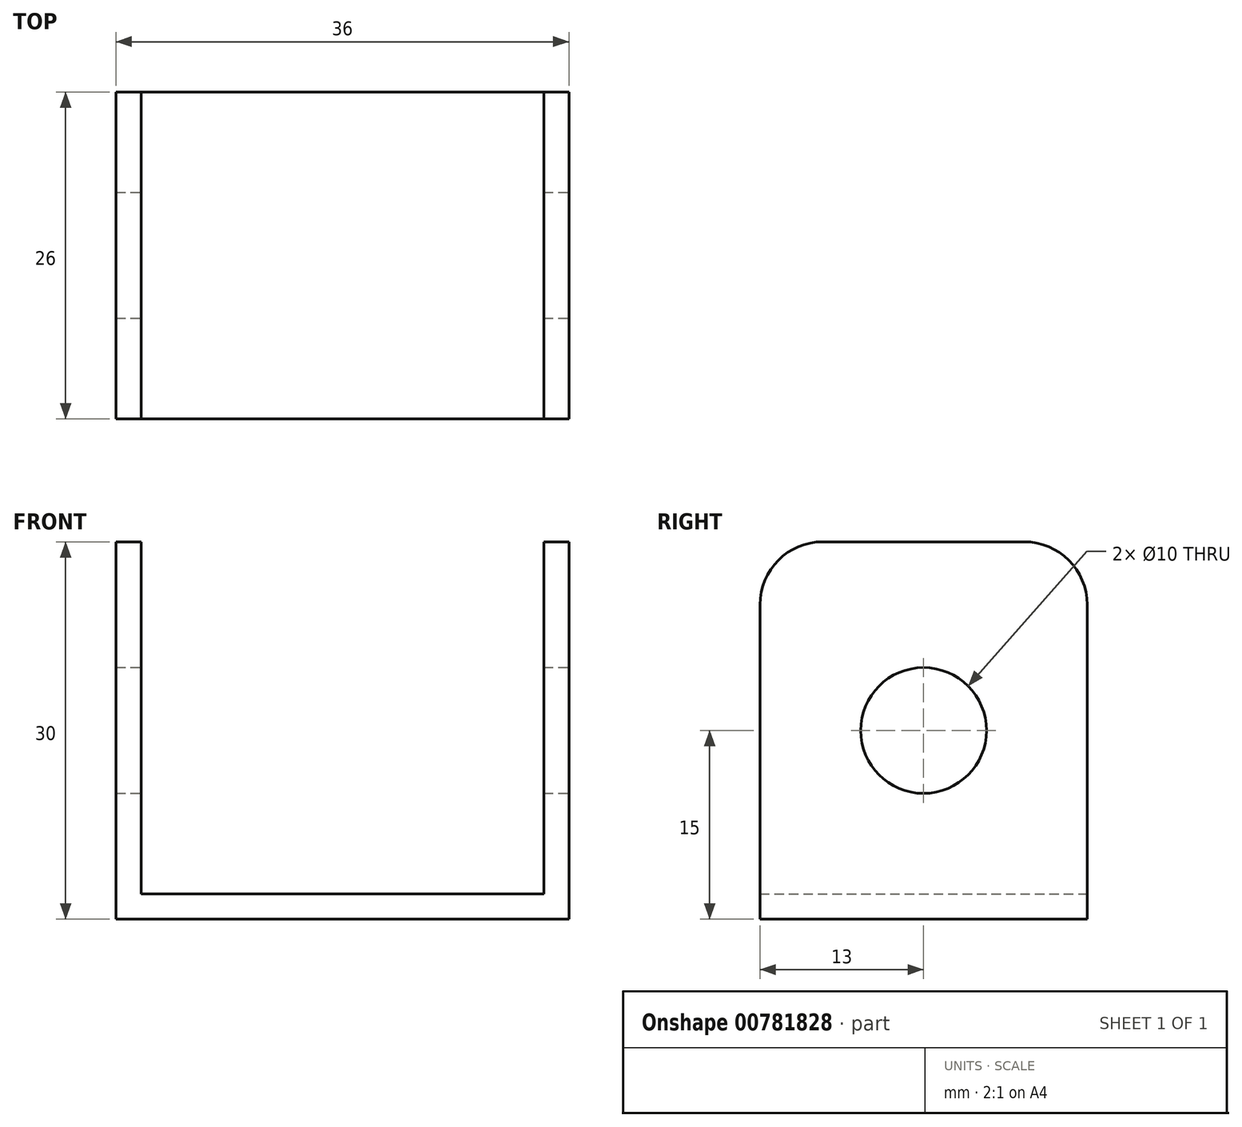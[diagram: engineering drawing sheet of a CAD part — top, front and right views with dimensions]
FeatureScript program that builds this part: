
annotation { "Feature Type Name" : "Feature", "Feature Type Description" : "" }
export const myFeature = defineFeature(function(context is Context, id is Id, definition is map)
    precondition{}
    {
        {
            var Q0;
            Q0=qCreatedBy(makeId("Front.planeOp"),FACE);
            var sketch = newSketch(context, id + "F0", { "sketchPlane" : qUnion([Q0])});
            skLineSegment(sketch, "E0.bottom", {"start": v(-18, 15) * mm, "end": v(-16, 15) * mm});
            skLineSegment(sketch, "E0.top", {"start": v(-18, -15) * mm, "end": v(18, -15) * mm});
            skLineSegment(sketch, "E0.left", {"start": v(-18, 15) * mm, "end": v(-18, -15) * mm});
            skLineSegment(sketch, "E0.right", {"start": v(18, 15) * mm, "end": v(18, -15) * mm});
            skPoint(sketch, "E0.middle", {"position": v(0, 0) * mm});
            skLineSegment(sketch, "E1.top", {"start": v(-16, -13) * mm, "end": v(16, -13) * mm});
            skLineSegment(sketch, "E1.left", {"start": v(-16, 13) * mm, "end": v(-16, -13) * mm});
            skLineSegment(sketch, "E1.right", {"start": v(16, 13) * mm, "end": v(16, -13) * mm});
            skLineSegment(sketch, "E2", {"start": v(-16, 13) * mm, "end": v(-16, 15) * mm});
            skLineSegment(sketch, "E3", {"start": v(16, 13) * mm, "end": v(16, 15) * mm});
            skLineSegment(sketch, "E4.trimOffspring", {"start": v(16, 15) * mm, "end": v(18, 15) * mm});
            skSolve(sketch);
        }
        {
            var Q0;
            Q0 = qSketchRegion(id + "F0", true);
            extrude(context, id + "F1", {"entities" : qUnion([Q0]), "depth" : 26 * mm, "offsetDistance" : 25 * mm});
        }
        {
            var Q0;
            Q0=makeQuery(id+"F1.opExtrude","SWEPT_FACE",FACE,{"disambiguationData":[OSD([sQuery(id+"F0.wireOp",EDGE,"E0.right")])]});
            var sketch = newSketch(context, id + "F2", { "sketchPlane" : qUnion([Q0])});
            skCircle(sketch, "E5", {"center": v(-13, 0) * mm, "radius": 5 * mm});
            skPoint(sketch, "E5.centerSnap0", {"position": v(-13, 15) * mm});
            skSolve(sketch);
        }
        {
            var Q0;
            Q0 = qSketchRegion(id + "F2", true);
            extrude(context, id + "F3", {"entities" : qUnion([Q0]), "operationType" : NewBodyOperationType.REMOVE, "endBound" : BoundingType.THROUGH_ALL, "oppositeDirection" : true, "depth" : 25 * mm, "offsetDistance" : 25 * mm});
        }
        {
            var Q0;
            Q0=makeQuery(id+"F1.opExtrude","CAP_EDGE",EDGE,{"disambiguationData":[OSD([sQuery(id+"F0.wireOp",EDGE,"E0.bottom")])],"isStart":false});
            var Q1;
            Q1=makeQuery(id+"F1.opExtrude","CAP_EDGE",EDGE,{"disambiguationData":[OSD([sQuery(id+"F0.wireOp",EDGE,"E0.bottom")])],"isStart":true});
            var Q2;
            Q2=makeQuery(id+"F1.opExtrude","CAP_EDGE",EDGE,{"disambiguationData":[OSD([sQuery(id+"F0.wireOp",EDGE,"E4.trimOffspring")])],"isStart":false});
            var Q3;
            Q3=makeQuery(id+"F1.opExtrude","CAP_EDGE",EDGE,{"disambiguationData":[OSD([sQuery(id+"F0.wireOp",EDGE,"E4.trimOffspring")])],"isStart":true});
            fillet(context, id + "F4", {"entities" : qUnion([Q0, Q1, Q2, Q3]), "radius" : 5 * mm, "tangentPropagation" : true, "allowEdgeOverflow" : false});
        }
    });
